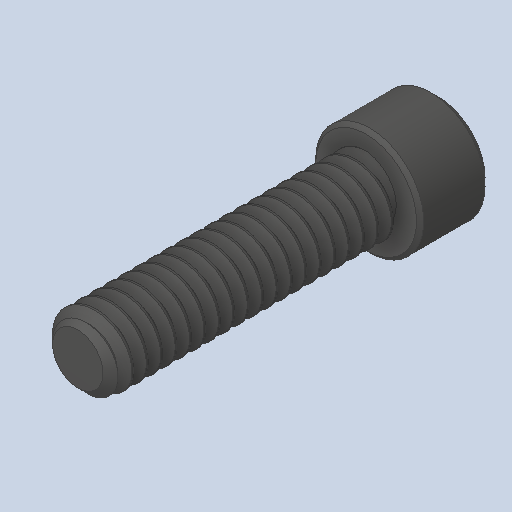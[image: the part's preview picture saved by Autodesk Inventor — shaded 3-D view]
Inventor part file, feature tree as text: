
AUTODESK INVENTOR PART (.ipt)
format: ipt  version: 2023 (Build 270158000, 158)  size: 705,024 bytes
history: native  units: in
note: dims shown in document units (in); Inventor stores cm internally (conversion verified against a paired STEP export)
features: chamfer x1
ambient origin geometry x8: Origin, YZ Plane, XZ Plane, XY Plane, X Axis, Y Axis, Z Axis, Center Point
bodies: Solid1 (feature_tree)
feature tree (1):
  chamfer  "Chamfer2"  [1 undecoded]
note: 1 required parameter value undecoded (feature->parameter linkage not recoverable at this tier; creation-order binding heuristic only, values carry confidence <= 0.55)
